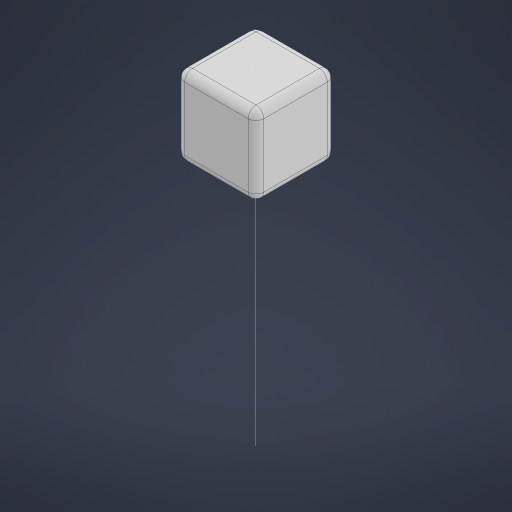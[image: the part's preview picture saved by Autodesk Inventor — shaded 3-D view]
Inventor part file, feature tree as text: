
AUTODESK INVENTOR PART (.ipt)
format: ipt  version: 2024.1 (Build 281209000, 209)  size: 2,139,136 bytes
history: native  units: mm
features: projected_geometry x5, fillet x4, other x3, extrude x3, sketch x3, boolean_combine x1, plane x1
ambient origin geometry x8: Origin, YZ Plane, XZ Plane, XY Plane, X Axis, Y Axis, Z Axis, Center Point
bodies: Solid2 (feature_tree), Solid1 (feature_tree)
feature tree (20):
  other  "TubeHolder YN Continuation.ipt"
  extrude  "Extrusion1"  Depth=30.0mm
  boolean_combine  "Combine1"
  plane  "Work Plane1"
  extrude  "Extrusion2"  Depth=10.0mm TaperAngle=0.0deg
  extrude  "Extrusion3"  TaperAngle=0.0deg  [1 undecoded]
  fillet  "Fillet1"  Radius=13.0mm
  fillet  "Fillet2"  Radius=6.0mm
  fillet  "Fillet3"  Radius=2.0mm
  fillet  "Fillet4"  Radius=1.5mm
  other  "Solid1::TubeHolder YN Continuation.ipt"
  other  "TaggingFeature1"
  sketch  "Sketch2"  dims[d0=10.0mm d1=30.0mm]
  projected_geometry  "Projected Loop1"
  projected_geometry  "Projected Loop2"
  projected_geometry  "Projected Loop3"
  projected_geometry  "Projected Loop4"
  sketch  "Sketch3"  dims[d2=30.0mm d3=10.0mm d4=20.0mm d5=0.0mm d6=0.0mm]
  sketch  "Sketch4"  dims[d7=-18.015mm d8=0.0mm d9=0.0mm d10=13.0mm d11=6.0mm d12=0.0mm d13=2.0mm d14=1.5mm d15=3.0mm d16=1.0mm]
  projected_geometry  "Project Cut Edges1"
note: 1 required parameter value undecoded (feature->parameter linkage not recoverable at this tier; creation-order binding heuristic only, values carry confidence <= 0.55)
